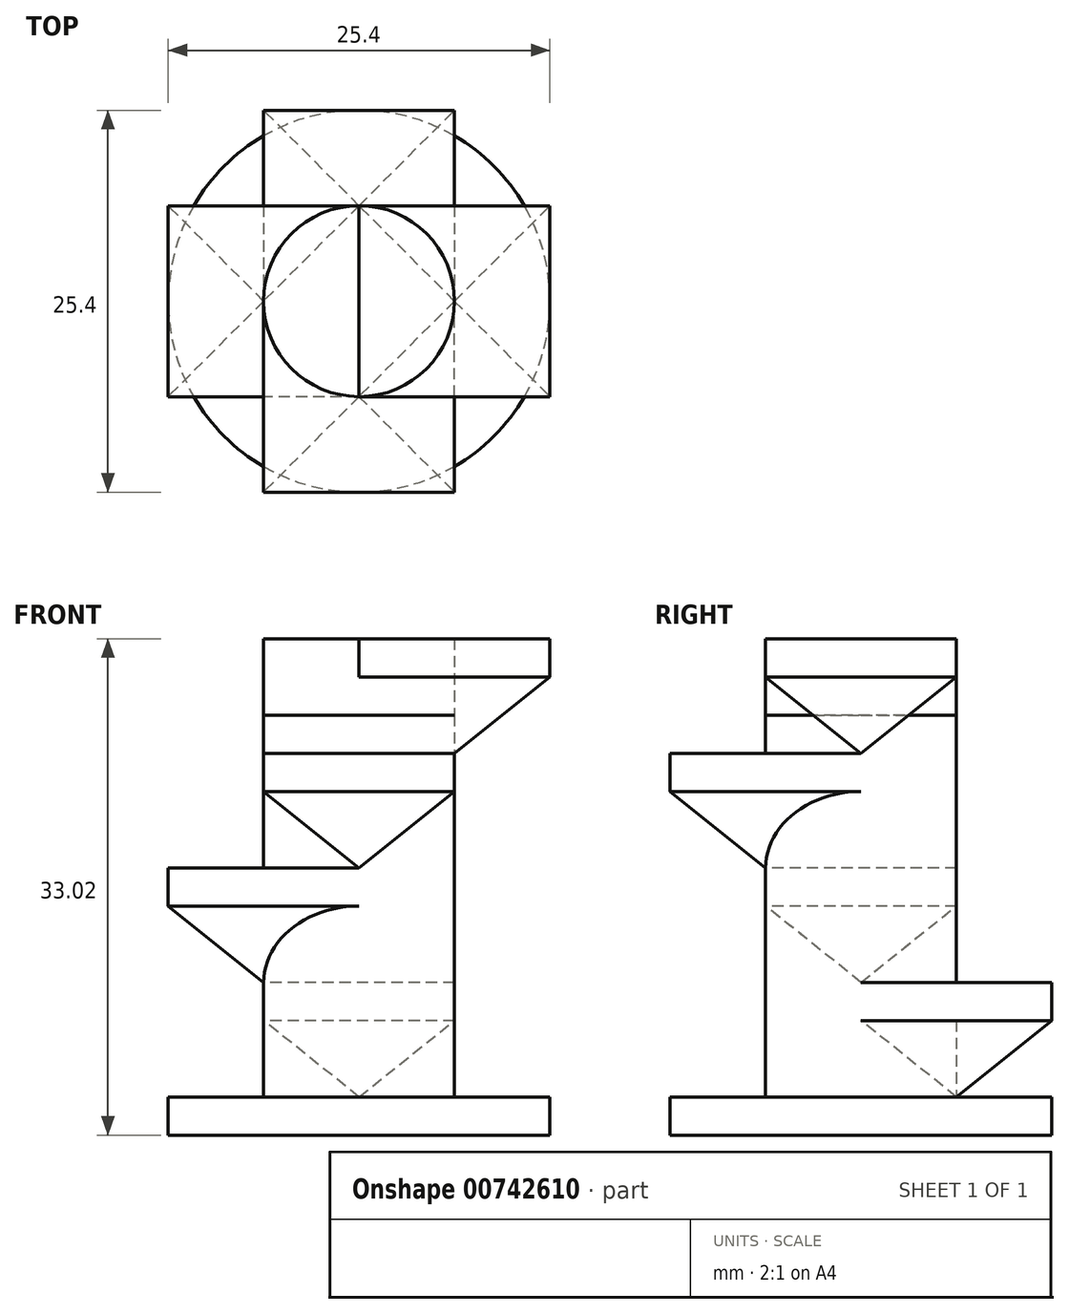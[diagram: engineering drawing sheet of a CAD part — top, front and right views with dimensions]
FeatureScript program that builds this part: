
annotation { "Feature Type Name" : "Feature", "Feature Type Description" : "" }
export const myFeature = defineFeature(function(context is Context, id is Id, definition is map)
    precondition{}
    {
        {
            var Q0;
            Q0=qCreatedBy(makeId("Top.planeOp"),FACE);
            var sketch = newSketch(context, id + "F0", { "sketchPlane" : qUnion([Q0])});
            skCircle(sketch, "E0", {"center": v(0, 0) * mm, "radius": 12.7 * mm});
            skSolve(sketch);
        }
        {
            var Q0;
            Q0 = qSketchRegion(id + "F0", true);
            extrude(context, id + "F1", {"entities" : qUnion([Q0]), "depth" : 2.54 * mm, "offsetDistance" : 25.4 * mm});
        }
        {
            var Q0;
            Q0=makeQuery(id+"F1.opExtrude","CAP_FACE",FACE,{"disambiguationData":[OSD([sQuery(id+"F0.wireOp",EDGE,"E0")])],"isStart":false});
            cPlane(context, id + "F2", {"entities" : qUnion([Q0]), "cplaneType" : CPlaneType.OFFSET, "offset" : 0 * mm, "width" : 152.4 * mm, "height" : 152.4 * mm});
        }
        {
            var Q0;
            Q0=qCreatedBy(id+"F2.planeOp",FACE);
            cPlane(context, id + "F3", {"entities" : qUnion([Q0]), "cplaneType" : CPlaneType.OFFSET, "offset" : 5.08 * mm, "width" : 152.4 * mm, "height" : 152.4 * mm});
        }
        {
            var Q0;
            Q0=qCreatedBy(id+"F3.planeOp",FACE);
            var sketch = newSketch(context, id + "F4", { "sketchPlane" : qUnion([Q0])});
            skLineSegment(sketch, "E1.bottom", {"start": v(6.35, 12.7) * mm, "end": v(-6.35, 12.7) * mm});
            skLineSegment(sketch, "E1.top", {"start": v(6.35, 0) * mm, "end": v(-6.35, 0) * mm});
            skLineSegment(sketch, "E1.left", {"start": v(6.35, 12.7) * mm, "end": v(6.35, 0) * mm});
            skLineSegment(sketch, "E1.right", {"start": v(-6.35, 12.7) * mm, "end": v(-6.35, 0) * mm});
            skPoint(sketch, "E1.middle", {"position": v(0, 6.35) * mm});
            skSolve(sketch);
        }
        {
            var Q0;
            Q0=makeQuery(id+"F4.imprint","IMPRINT",FACE,{"disambiguationData":[TD([[makeQuery(id+"F4.imprint","IMPRINT",EDGE,{"derivedFrom":sQuery(id+"F4.wireOp",EDGE,"E1.bottom")}),1.0]])]});
            extrude(context, id + "F5", {"entities" : qUnion([Q0]), "depth" : 2.54 * mm, "offsetDistance" : 25.4 * mm});
        }
        {
            var Q0;
            Q0=makeQuery(id+"F1.opExtrude","CAP_FACE",FACE,{"disambiguationData":[OSD([sQuery(id+"F0.wireOp",EDGE,"E0")])],"isStart":false});
            var sketch = newSketch(context, id + "F6", { "sketchPlane" : qUnion([Q0])});
            skCircle(sketch, "E2", {"center": v(0, 0) * mm, "radius": 6.35 * mm});
            skSolve(sketch);
        }
        {
            var Q0;
            Q0=makeQuery(id+"F6.imprint","IMPRINT",FACE,{"disambiguationData":[TD([[makeQuery(id+"F6.imprint","IMPRINT",EDGE,{"derivedFrom":sQuery(id+"F6.wireOp",EDGE,"E2")}),1.0]])]});
            extrude(context, id + "F7", {"entities" : qUnion([Q0]), "depth" : 25.4 * mm, "offsetDistance" : 25.4 * mm});
        }
        {
            var Q0;
            Q0=makeQuery(id+"F5.opExtrude","CAP_FACE",FACE,{"disambiguationData":[OSD([sQuery(id+"F4.wireOp",EDGE,"E1.bottom"),sQuery(id+"F4.wireOp",EDGE,"E1.top"),sQuery(id+"F4.wireOp",EDGE,"E1.left"),sQuery(id+"F4.wireOp",EDGE,"E1.right")])],"isStart":false});
            cPlane(context, id + "F8", {"entities" : qUnion([Q0]), "cplaneType" : CPlaneType.OFFSET, "offset" : 5.08 * mm, "width" : 152.4 * mm, "height" : 152.4 * mm});
        }
        {
            var Q0;
            Q0=qCreatedBy(id+"F8.planeOp",FACE);
            var sketch = newSketch(context, id + "F9", { "sketchPlane" : qUnion([Q0])});
            skLineSegment(sketch, "E3.bottom", {"start": v(0, 6.35) * mm, "end": v(-12.7, 6.35) * mm});
            skLineSegment(sketch, "E3.top", {"start": v(0, -6.35) * mm, "end": v(-12.7, -6.35) * mm});
            skLineSegment(sketch, "E3.left", {"start": v(0, 6.35) * mm, "end": v(0, -6.35) * mm});
            skLineSegment(sketch, "E3.right", {"start": v(-12.7, 6.35) * mm, "end": v(-12.7, -6.35) * mm});
            skSolve(sketch);
        }
        {
            var Q0;
            Q0=makeQuery(id+"F9.imprint","IMPRINT",FACE,{"disambiguationData":[TD([[makeQuery(id+"F9.imprint","IMPRINT",EDGE,{"derivedFrom":sQuery(id+"F9.wireOp",EDGE,"E3.bottom")}),1.0]])]});
            extrude(context, id + "F10", {"entities" : qUnion([Q0]), "operationType" : NewBodyOperationType.ADD, "depth" : 2.54 * mm, "offsetDistance" : 25.4 * mm});
        }
        {
            var Q0;
            Q0=makeQuery(id+"F5.opExtrude","CAP_FACE",FACE,{"disambiguationData":[OSD([sQuery(id+"F4.wireOp",EDGE,"E1.bottom"),sQuery(id+"F4.wireOp",EDGE,"E1.top"),sQuery(id+"F4.wireOp",EDGE,"E1.left"),sQuery(id+"F4.wireOp",EDGE,"E1.right")])],"isStart":false});
            var sketch = newSketch(context, id + "F11", { "sketchPlane" : qUnion([Q0])});
            skPoint(sketch, "E4", {"position": v(-6.35, 0) * mm});
            skSolve(sketch);
        }
        {
            var Q1;
            Q1=sQuery(id+"F11.wireOp",VERTEX,"E4");
            var Q2;
            Q2=makeQuery(id+"F10.opExtrude","CAP_FACE",FACE,{"disambiguationData":[OSD([sQuery(id+"F9.wireOp",EDGE,"E3.bottom"),sQuery(id+"F9.wireOp",EDGE,"E3.top"),sQuery(id+"F9.wireOp",EDGE,"E3.left"),sQuery(id+"F9.wireOp",EDGE,"E3.right")])],"isStart":true});
            loft(context, id + "F12", {"operationType" : NewBodyOperationType.ADD, "sheetProfilesArray" : [{ "sheetProfileEntities" : qUnion([Q1]) }, { "sheetProfileEntities" : qUnion([Q2]) }]});
        }
        {
            var Q0;
            Q0=makeQuery(id+"F1.opExtrude","CAP_FACE",FACE,{"disambiguationData":[OSD([sQuery(id+"F0.wireOp",EDGE,"E0")])],"isStart":false});
            var sketch = newSketch(context, id + "F13", { "sketchPlane" : qUnion([Q0])});
            skPoint(sketch, "E5", {"position": v(0, 6.35) * mm});
            skSolve(sketch);
        }
        {
            var Q0;
            Q0=sQuery(id+"F13.wireOp",VERTEX,"E5");
            var Q1;
            Q1=makeQuery(id+"F5.opExtrude","CAP_FACE",FACE,{"disambiguationData":[OSD([sQuery(id+"F4.wireOp",EDGE,"E1.bottom"),sQuery(id+"F4.wireOp",EDGE,"E1.top"),sQuery(id+"F4.wireOp",EDGE,"E1.left"),sQuery(id+"F4.wireOp",EDGE,"E1.right")])],"isStart":true});
            loft(context, id + "F14", {"sheetProfilesArray" : [{ "sheetProfileEntities" : qUnion([Q0]) }, { "sheetProfileEntities" : qUnion([Q1]) }]});
        }
        {
            var Q0;
            Q0=makeQuery(id+"F10.opExtrude","CAP_FACE",FACE,{"disambiguationData":[OSD([sQuery(id+"F9.wireOp",EDGE,"E3.bottom"),sQuery(id+"F9.wireOp",EDGE,"E3.top"),sQuery(id+"F9.wireOp",EDGE,"E3.left"),sQuery(id+"F9.wireOp",EDGE,"E3.right")])],"isStart":false});
            cPlane(context, id + "F15", {"entities" : qUnion([Q0]), "cplaneType" : CPlaneType.OFFSET, "offset" : 5.08 * mm, "width" : 152.4 * mm, "height" : 152.4 * mm});
        }
        {
            var Q0;
            Q0=qCreatedBy(id+"F15.planeOp",FACE);
            var sketch = newSketch(context, id + "F16", { "sketchPlane" : qUnion([Q0])});
            skLineSegment(sketch, "E6.bottom", {"start": v(6.35, -12.7) * mm, "end": v(-6.35, -12.7) * mm});
            skLineSegment(sketch, "E6.top", {"start": v(6.35, 0) * mm, "end": v(-6.35, 0) * mm});
            skLineSegment(sketch, "E6.left", {"start": v(6.35, -12.7) * mm, "end": v(6.35, 0) * mm});
            skLineSegment(sketch, "E6.right", {"start": v(-6.35, -12.7) * mm, "end": v(-6.35, 0) * mm});
            skPoint(sketch, "E6.middle", {"position": v(0, -6.35) * mm});
            skSolve(sketch);
        }
        {
            var Q0;
            Q0=makeQuery(id+"F16.imprint","IMPRINT",FACE,{"disambiguationData":[TD([[makeQuery(id+"F16.imprint","IMPRINT",EDGE,{"derivedFrom":sQuery(id+"F16.wireOp",EDGE,"E6.bottom")}),-1.0]])]});
            extrude(context, id + "F17", {"entities" : qUnion([Q0]), "operationType" : NewBodyOperationType.ADD, "depth" : 2.54 * mm, "offsetDistance" : 25.4 * mm});
        }
        {
            var Q0;
            Q0=makeQuery(id+"F10.opExtrude","CAP_FACE",FACE,{"disambiguationData":[OSD([sQuery(id+"F9.wireOp",EDGE,"E3.bottom"),sQuery(id+"F9.wireOp",EDGE,"E3.top"),sQuery(id+"F9.wireOp",EDGE,"E3.left"),sQuery(id+"F9.wireOp",EDGE,"E3.right")])],"isStart":false});
            var sketch = newSketch(context, id + "F18", { "sketchPlane" : qUnion([Q0])});
            skPoint(sketch, "E7", {"position": v(0, -6.35) * mm});
            skSolve(sketch);
        }
        {
            var Q1;
            Q1=sQuery(id+"F18.wireOp",VERTEX,"E7");
            var Q2;
            Q2=makeQuery(id+"F17.opExtrude","CAP_FACE",FACE,{"disambiguationData":[OSD([sQuery(id+"F16.wireOp",EDGE,"E6.bottom"),sQuery(id+"F16.wireOp",EDGE,"E6.top"),sQuery(id+"F16.wireOp",EDGE,"E6.left"),sQuery(id+"F16.wireOp",EDGE,"E6.right")])],"isStart":true});
            loft(context, id + "F19", {"operationType" : NewBodyOperationType.ADD, "sheetProfilesArray" : [{ "sheetProfileEntities" : qUnion([Q1]) }, { "sheetProfileEntities" : qUnion([Q2]) }]});
        }
        {
            var Q0;
            Q0=makeQuery(id+"F17.opExtrude","CAP_FACE",FACE,{"disambiguationData":[OSD([sQuery(id+"F16.wireOp",EDGE,"E6.bottom"),sQuery(id+"F16.wireOp",EDGE,"E6.top"),sQuery(id+"F16.wireOp",EDGE,"E6.left"),sQuery(id+"F16.wireOp",EDGE,"E6.right")])],"isStart":false});
            cPlane(context, id + "F20", {"entities" : qUnion([Q0]), "cplaneType" : CPlaneType.OFFSET, "offset" : 5.08 * mm, "width" : 152.4 * mm, "height" : 152.4 * mm});
        }
        {
            var Q0;
            Q0=qCreatedBy(id+"F20.planeOp",FACE);
            var sketch = newSketch(context, id + "F21", { "sketchPlane" : qUnion([Q0])});
            skLineSegment(sketch, "E8.bottom", {"start": v(12.7, 6.35) * mm, "end": v(0, 6.35) * mm});
            skLineSegment(sketch, "E8.top", {"start": v(12.7, -6.35) * mm, "end": v(0, -6.35) * mm});
            skLineSegment(sketch, "E8.left", {"start": v(12.7, 6.35) * mm, "end": v(12.7, -6.35) * mm});
            skLineSegment(sketch, "E8.right", {"start": v(0, 6.35) * mm, "end": v(0, -6.35) * mm});
            skPoint(sketch, "E8.middle", {"position": v(6.35, 0) * mm});
            skSolve(sketch);
        }
        {
            var Q0;
            Q0=makeQuery(id+"F21.imprint","IMPRINT",FACE,{"disambiguationData":[TD([[makeQuery(id+"F21.imprint","IMPRINT",EDGE,{"derivedFrom":sQuery(id+"F21.wireOp",EDGE,"E8.bottom")}),1.0]])]});
            extrude(context, id + "F22", {"entities" : qUnion([Q0]), "depth" : 2.54 * mm, "offsetDistance" : 25.4 * mm});
        }
        {
            var Q0;
            Q0=makeQuery(id+"F7.opExtrude","CAP_FACE",FACE,{"disambiguationData":[OSD([sQuery(id+"F6.wireOp",EDGE,"E2")])],"isStart":false});
            var sketch = newSketch(context, id + "F23", { "sketchPlane" : qUnion([Q0])});
            skCircle(sketch, "E9", {"center": v(0, 0) * mm, "radius": 6.35 * mm});
            skSolve(sketch);
        }
        {
            var Q0;
            Q0=makeQuery(id+"F23.imprint","IMPRINT",FACE,{"disambiguationData":[TD([[makeQuery(id+"F23.imprint","IMPRINT",EDGE,{"derivedFrom":sQuery(id+"F23.wireOp",EDGE,"E9")}),1.0]])]});
            var Q1;
            Q1=makeQuery(id+"F22.opExtrude","CAP_FACE",FACE,{"disambiguationData":[OSD([sQuery(id+"F21.wireOp",EDGE,"E8.bottom"),sQuery(id+"F21.wireOp",EDGE,"E8.top"),sQuery(id+"F21.wireOp",EDGE,"E8.left"),sQuery(id+"F21.wireOp",EDGE,"E8.right")])],"isStart":false});
            extrude(context, id + "F24", {"entities" : qUnion([Q0]), "endBound" : BoundingType.UP_TO_SURFACE, "depth" : 25.4 * mm, "endBoundEntityFace" : qUnion([Q1]), "offsetDistance" : 25.4 * mm});
        }
        {
            var Q0;
            Q0=makeQuery(id+"F17.opExtrude","CAP_FACE",FACE,{"disambiguationData":[OSD([sQuery(id+"F16.wireOp",EDGE,"E6.bottom"),sQuery(id+"F16.wireOp",EDGE,"E6.top"),sQuery(id+"F16.wireOp",EDGE,"E6.left"),sQuery(id+"F16.wireOp",EDGE,"E6.right")])],"isStart":false});
            var sketch = newSketch(context, id + "F25", { "sketchPlane" : qUnion([Q0])});
            skPoint(sketch, "E10", {"position": v(6.35, 0) * mm});
            skSolve(sketch);
        }
        {
            var Q0;
            Q0=sQuery(id+"F25.wireOp",VERTEX,"E10");
            var Q1;
            Q1=makeQuery(id+"F22.opExtrude","CAP_FACE",FACE,{"disambiguationData":[OSD([sQuery(id+"F21.wireOp",EDGE,"E8.bottom"),sQuery(id+"F21.wireOp",EDGE,"E8.top"),sQuery(id+"F21.wireOp",EDGE,"E8.left"),sQuery(id+"F21.wireOp",EDGE,"E8.right")])],"isStart":true});
            loft(context, id + "F26", {"sheetProfilesArray" : [{ "sheetProfileEntities" : qUnion([Q0]) }, { "sheetProfileEntities" : qUnion([Q1]) }]});
        }
    });
